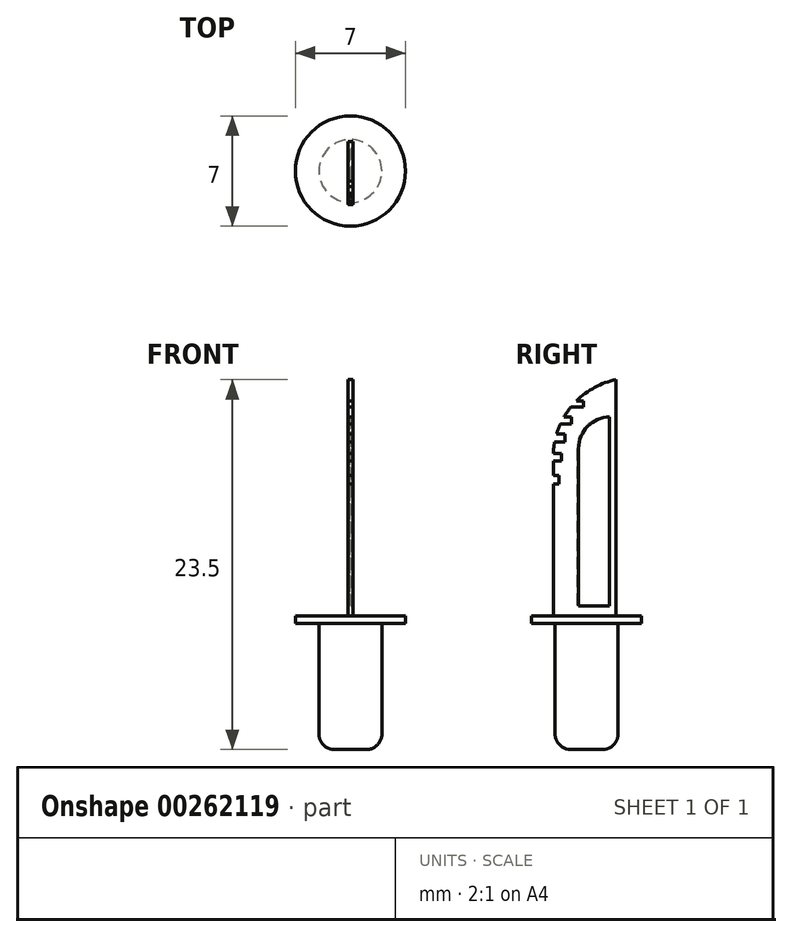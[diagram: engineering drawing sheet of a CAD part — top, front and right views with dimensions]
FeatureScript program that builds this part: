
annotation { "Feature Type Name" : "Feature", "Feature Type Description" : "" }
export const myFeature = defineFeature(function(context is Context, id is Id, definition is map)
    precondition{}
    {
        {
            var Q0;
            Q0=qCreatedBy(makeId("Top.planeOp"),FACE);
            var sketch = newSketch(context, id + "F0", { "sketchPlane" : qUnion([Q0])});
            skCircle(sketch, "E0", {"center": v(0, 0) * mm, "radius": 2 * mm});
            skSolve(sketch);
        }
        {
            var Q0;
            Q0 = qSketchRegion(id + "F0", true);
            extrude(context, id + "F1", {"entities" : qUnion([Q0]), "depth" : 8 * mm});
        }
        {
            var Q0;
            Q0=makeQuery(id+"F1.opExtrude","CAP_FACE",FACE,{"disambiguationData":[OSD([sQuery(id+"F0.wireOp",EDGE,"E0")])],"isStart":false});
            var sketch = newSketch(context, id + "F2", { "sketchPlane" : qUnion([Q0])});
            skCircle(sketch, "E1", {"center": v(0, 0) * mm, "radius": 3.5 * mm});
            skSolve(sketch);
        }
        {
            var Q0;
            Q0=makeQuery(id+"F2.imprint","IMPRINT",FACE,{"disambiguationData":[TD([[makeQuery(id+"F2.imprint","IMPRINT",EDGE,{"derivedFrom":sQuery(id+"F2.wireOp",EDGE,"E1")}),1.0]])]});
            var Q1;
            Q1=makeQuery(id+"F2.imprint","IMPRINT",FACE,{"disambiguationData":[TD([[makeQuery(id+"F2.imprint","IMPRINT",EDGE,{"derivedFrom":makeQuery(id+"F1.opExtrude","CAP_EDGE",EDGE,{"disambiguationData":[OSD([sQuery(id+"F0.wireOp",EDGE,"E0")])],"isStart":false})}),1.0]])]});
            extrude(context, id + "F3", {"entities" : qUnion([Q0, Q1]), "operationType" : NewBodyOperationType.ADD, "depth" : .5 * mm});
        }
        {
            var Q0;
            Q0=makeQuery(id+"F3.opExtrude","CAP_FACE",FACE,{"disambiguationData":[OSD([sQuery(id+"F2.wireOp",EDGE,"E1")])],"isStart":false});
            var sketch = newSketch(context, id + "F4", { "sketchPlane" : qUnion([Q0])});
            skLineSegment(sketch, "E2.bottom", {"start": v(-0.15, 1.87) * mm, "end": v(0.15, 1.87) * mm});
            skLineSegment(sketch, "E2.top", {"start": v(-0.15, -2.12) * mm, "end": v(0.15, -2.12) * mm});
            skLineSegment(sketch, "E2.left", {"start": v(-0.15, 1.87) * mm, "end": v(-0.15, -2.12) * mm});
            skLineSegment(sketch, "E2.right", {"start": v(0.15, 1.87) * mm, "end": v(0.15, -2.12) * mm});
            skLineSegment(sketch, "E3", {"start": v(0, 0) * mm, "end": v(0, 3.5) * mm, "construction": true});
            skSolve(sketch);
        }
        {
            var Q0;
            Q0 = qSketchRegion(id + "F4", true);
            extrude(context, id + "F5", {"entities" : qUnion([Q0]), "operationType" : NewBodyOperationType.ADD, "depth" : 15 * mm});
        }
        {
            var Q0;
            Q0=makeQuery(id+"F5.opExtrude","CAP_EDGE",EDGE,{"disambiguationData":[OSD([sQuery(id+"F4.wireOp",EDGE,"E2.top")])],"isStart":false});
            fillet(context, id + "F6", {"entities" : qUnion([Q0]), "radius" : 5 * mm, "tangentPropagation" : true, "allowEdgeOverflow" : false});
        }
        {
            var Q0;
            Q0=makeQuery(id+"F1.opExtrude","CAP_EDGE",EDGE,{"disambiguationData":[OSD([sQuery(id+"F0.wireOp",EDGE,"E0")])],"isStart":true});
            fillet(context, id + "F7", {"entities" : qUnion([Q0]), "radius" : 1 * mm, "tangentPropagation" : true, "allowEdgeOverflow" : false});
        }
        {
            var Q0;
            Q0=makeQuery(id+"F5.opExtrude","SWEPT_FACE",FACE,{"disambiguationData":[OSD([sQuery(id+"F4.wireOp",EDGE,"E2.left")])]});
            var sketch = newSketch(context, id + "F8", { "sketchPlane" : qUnion([Q0])});
            skLineSegment(sketch, "E4.bottom", {"start": v(3.03, 20.05) * mm, "end": v(1.38, 20.05) * mm});
            skLineSegment(sketch, "E4.top", {"start": v(3.03, 19.55) * mm, "end": v(1.38, 19.55) * mm});
            skLineSegment(sketch, "E4.left", {"start": v(3.03, 20.05) * mm, "end": v(3.03, 19.55) * mm});
            skLineSegment(sketch, "E4.right", {"start": v(1.38, 20.05) * mm, "end": v(1.38, 19.55) * mm});
            skLineSegment(sketch, "E5.bottom", {"start": v(2.86, 18.8) * mm, "end": v(1.58, 18.8) * mm});
            skLineSegment(sketch, "E5.top", {"start": v(2.86, 18.32) * mm, "end": v(1.58, 18.32) * mm});
            skLineSegment(sketch, "E5.left", {"start": v(2.86, 18.8) * mm, "end": v(2.86, 18.32) * mm});
            skLineSegment(sketch, "E5.right", {"start": v(1.58, 18.8) * mm, "end": v(1.58, 18.32) * mm});
            skLineSegment(sketch, "E6.bottom", {"start": v(2.23, 21.14) * mm, "end": v(0.94, 21.14) * mm});
            skLineSegment(sketch, "E6.top", {"start": v(2.23, 20.68) * mm, "end": v(0.94, 20.68) * mm});
            skLineSegment(sketch, "E6.left", {"start": v(2.23, 21.14) * mm, "end": v(2.23, 20.68) * mm});
            skLineSegment(sketch, "E6.right", {"start": v(0.94, 21.14) * mm, "end": v(0.94, 20.68) * mm});
            skPoint(sketch, "E7.firstSnap0", {"position": v(1, 21.76) * mm});
            skPoint(sketch, "E7.oppositeSnap0", {"position": v(1, 21.76) * mm});
            skLineSegment(sketch, "E7.bottom", {"start": v(1, 22.15) * mm, "end": v(0.2, 22.15) * mm});
            skLineSegment(sketch, "E7.top", {"start": v(1, 21.76) * mm, "end": v(0.2, 21.76) * mm});
            skLineSegment(sketch, "E7.left", {"start": v(1, 22.15) * mm, "end": v(1, 21.76) * mm});
            skLineSegment(sketch, "E7.right", {"start": v(0.2, 22.15) * mm, "end": v(0.2, 21.76) * mm});
            skLineSegment(sketch, "E8.bottom", {"start": v(3.03, 17.42) * mm, "end": v(1.75, 17.42) * mm});
            skLineSegment(sketch, "E8.top", {"start": v(3.03, 16.88) * mm, "end": v(1.75, 16.88) * mm});
            skLineSegment(sketch, "E8.left", {"start": v(3.03, 17.42) * mm, "end": v(3.03, 16.88) * mm});
            skLineSegment(sketch, "E8.right", {"start": v(1.75, 17.42) * mm, "end": v(1.75, 16.88) * mm});
            skSolve(sketch);
        }
        {
            var Q0;
            Q0 = qSketchRegion(id + "F8", true);
            extrude(context, id + "F9", {"entities" : qUnion([Q0]), "operationType" : NewBodyOperationType.REMOVE, "oppositeDirection" : true, "depth" : .3 * mm});
        }
        {
            var Q0;
            Q0=makeQuery(id+"F5.opExtrude","SWEPT_FACE",FACE,{"disambiguationData":[OSD([sQuery(id+"F4.wireOp",EDGE,"E2.left")])]});
            var sketch = newSketch(context, id + "F10", { "sketchPlane" : qUnion([Q0])});
            skLineSegment(sketch, "E9.bottom", {"start": v(-1.4, 21.13) * mm, "end": v(-1.4, 21.13) * mm});
            skLineSegment(sketch, "E9.top", {"start": v(-1.4, 9.13) * mm, "end": v(0.6, 9.13) * mm});
            skLineSegment(sketch, "E9.left", {"start": v(-1.4, 21.13) * mm, "end": v(-1.4, 9.13) * mm});
            skLineSegment(sketch, "E9.right", {"start": v(0.6, 19.13) * mm, "end": v(0.6, 9.13) * mm});
            skPoint(sketch, "E10.visualSharp", {"position": v(0.6, 21.13) * mm});
            skArc(sketch, "E10.filletArc", {"start": v(0.6, 19.13) * mm, "mid": v(0.01, 20.54) * mm, "end": v(-1.4, 21.13) * mm});
            skSolve(sketch);
        }
        {
            var Q0;
            Q0=makeQuery(id+"F10.imprint","IMPRINT",FACE,{"disambiguationData":[TD([[makeQuery(id+"F10.imprint","IMPRINT",EDGE,{"derivedFrom":sQuery(id+"F10.wireOp",EDGE,"E9.top")}),1.0]])]});
            extrude(context, id + "F11", {"entities" : qUnion([Q0]), "operationType" : NewBodyOperationType.REMOVE, "oppositeDirection" : true, "depth" : .1 * mm});
        }
        {
            var Q0;
            Q0=makeQuery(id+"F5.opExtrude","SWEPT_FACE",FACE,{"disambiguationData":[OSD([sQuery(id+"F4.wireOp",EDGE,"E2.right")])]});
            var sketch = newSketch(context, id + "F12", { "sketchPlane" : qUnion([Q0])});
            skLineSegment(sketch, "E11.bottom", {"start": v(1.46, 9.11) * mm, "end": v(-0.5, 9.11) * mm});
            skLineSegment(sketch, "E11.top", {"start": v(1.5, 21.13) * mm, "end": v(1.46, 21.13) * mm});
            skLineSegment(sketch, "E11.left", {"start": v(1.46, 9.11) * mm, "end": v(1.46, 21.13) * mm});
            skLineSegment(sketch, "E11.right", {"start": v(-0.5, 9.11) * mm, "end": v(-0.5, 19.13) * mm});
            skPoint(sketch, "E12.visualSharp", {"position": v(-0.5, 21.13) * mm});
            skArc(sketch, "E12.filletArc", {"start": v(1.5, 21.13) * mm, "mid": v(0.08, 20.54) * mm, "end": v(-0.5, 19.13) * mm});
            skSolve(sketch);
        }
        {
            var Q0;
            {var subQ0=sQuery(id+"F12.wireOp",EDGE,"E11.bottom");Q0=makeQuery(id+"F12.imprint","IMPRINT",FACE,{"disambiguationData":[TD([[makeQuery(id+"F12.imprint","IMPRINT",EDGE,{"derivedFrom":subQ0}),-1.0]])]});}
            extrude(context, id + "F13", {"entities" : qUnion([Q0]), "operationType" : NewBodyOperationType.REMOVE, "oppositeDirection" : true, "depth" : .1 * mm});
        }
    });
